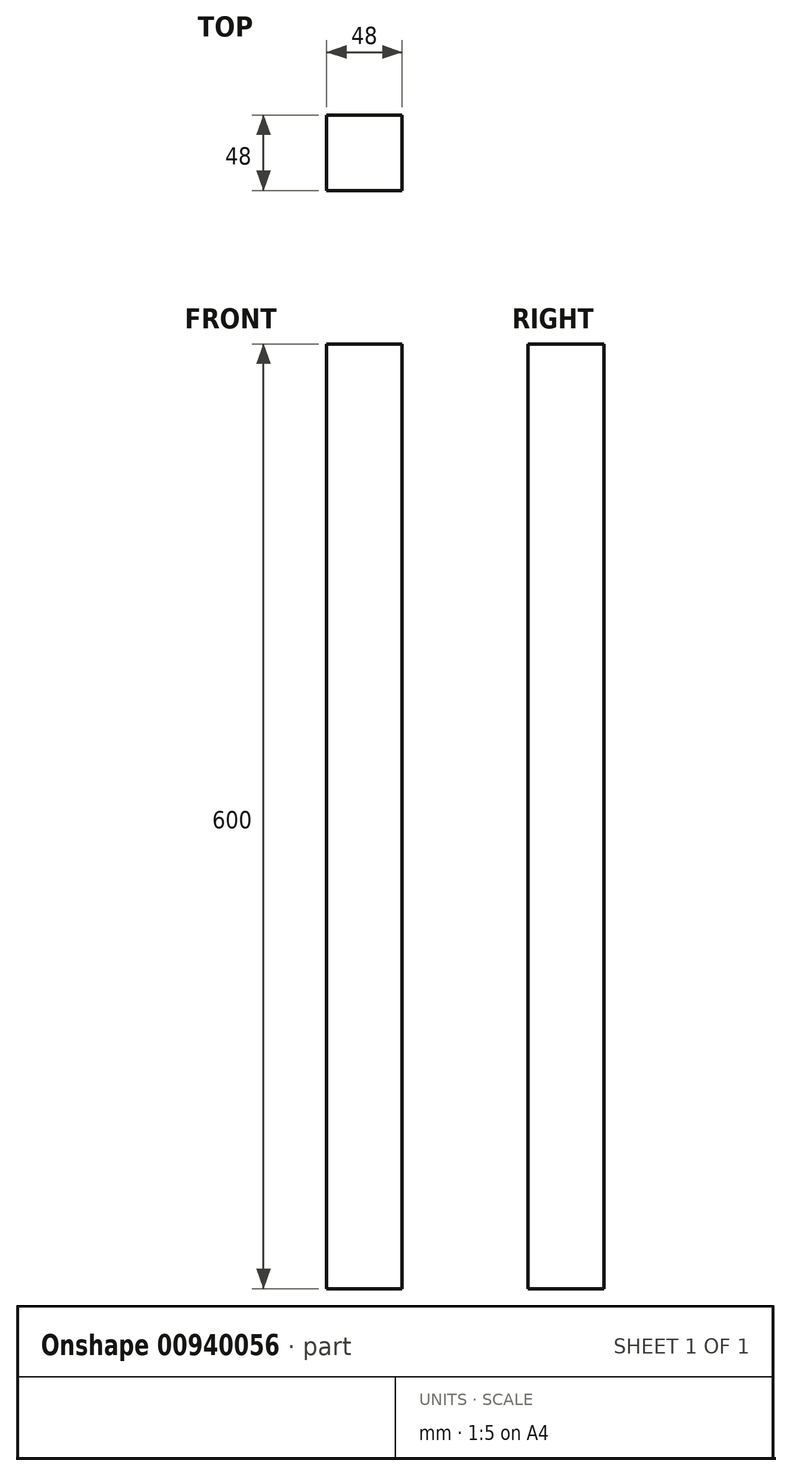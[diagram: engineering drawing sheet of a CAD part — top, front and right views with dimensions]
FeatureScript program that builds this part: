
annotation { "Feature Type Name" : "Feature", "Feature Type Description" : "" }
export const myFeature = defineFeature(function(context is Context, id is Id, definition is map)
    precondition{}
    {
        {
            var Q0;
            Q0=qCreatedBy(makeId("Top.planeOp"),FACE);
            var sketch = newSketch(context, id + "F0", { "sketchPlane" : qUnion([Q0])});
            skLineSegment(sketch, "E0.bottom", {"start": v(24, 24) * mm, "end": v(-24, 24) * mm});
            skLineSegment(sketch, "E0.top", {"start": v(24, -24) * mm, "end": v(-24, -24) * mm});
            skLineSegment(sketch, "E0.left", {"start": v(24, 24) * mm, "end": v(24, -24) * mm});
            skLineSegment(sketch, "E0.right", {"start": v(-24, 24) * mm, "end": v(-24, -24) * mm});
            skPoint(sketch, "E0.middle", {"position": v(0, 0) * mm});
            skSolve(sketch);
        }
        {
            var Q0;
            Q0 = qSketchRegion(id + "F0", true);
            extrude(context, id + "F1", {"entities" : qUnion([Q0]), "depth" : 600 * mm, "offsetDistance" : 25 * mm});
        }
    });
